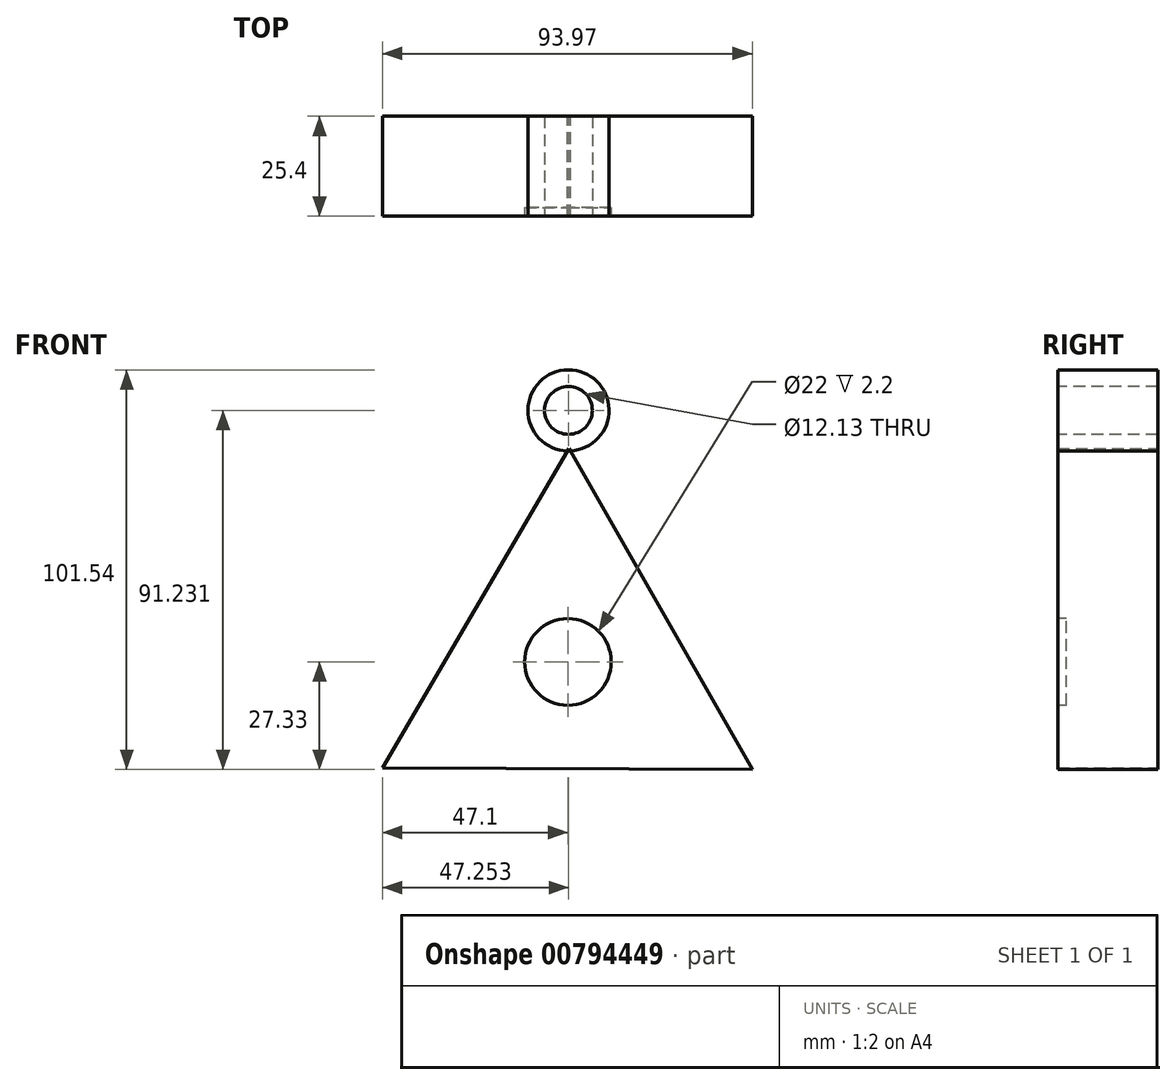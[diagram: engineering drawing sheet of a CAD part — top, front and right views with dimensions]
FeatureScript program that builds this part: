
annotation { "Feature Type Name" : "Feature", "Feature Type Description" : "" }
export const myFeature = defineFeature(function(context is Context, id is Id, definition is map)
    precondition{}
    {
        {
            var Q0;
            Q0=qCreatedBy(makeId("Front.planeOp"),FACE);
            var sketch = newSketch(context, id + "F0", { "sketchPlane" : qUnion([Q0])});
            skCircle(sketch, "E0.cCircle", {"center": v(0, 0) * mm, "radius": 27.13 * mm, "construction": true});
            skLineSegment(sketch, "E0.0", {"start": v(0.23, 54.25) * mm, "end": v(46.87, -27.33) * mm});
            skLineSegment(sketch, "E0.1", {"start": v(46.87, -27.33) * mm, "end": v(-47.1, -26.93) * mm});
            skLineSegment(sketch, "E0.2", {"start": v(-47.1, -26.93) * mm, "end": v(0.23, 54.25) * mm});
            skPoint(sketch, "E0.0.midPoint", {"position": v(23.55, 13.46) * mm});
            skCircle(sketch, "E1", {"center": v(0.15, 63.9) * mm, "radius": 10.3 * mm});
            skSolve(sketch);
        }
        {
            var Q0;
            Q0=makeQuery(id+"F0.imprint","IMPRINT",FACE,{"disambiguationData":[TD([[makeQuery(id+"F0.imprint","IMPRINT",EDGE,{"derivedFrom":sQuery(id+"F0.wireOp",EDGE,"E0.0")}),-1.0]])]});
            extrude(context, id + "F1", {"entities" : qUnion([Q0]), "depth" : 25.4 * mm, "offsetDistance" : 25.4 * mm});
        }
        {
            var Q0;
            Q0=makeQuery(id+"F1.opExtrude","CAP_FACE",FACE,{"disambiguationData":[OSD([sQuery(id+"F0.wireOp",EDGE,"E0.0"),sQuery(id+"F0.wireOp",EDGE,"E0.1"),sQuery(id+"F0.wireOp",EDGE,"E0.2")])],"isStart":false});
            var sketch = newSketch(context, id + "F2", { "sketchPlane" : qUnion([Q0])});
            skCircle(sketch, "E2", {"center": v(0, 0) * mm, "radius": 11 * mm});
            skSolve(sketch);
        }
        {
            var Q0;
            Q0=makeQuery(id+"F2.imprint","IMPRINT",FACE,{"disambiguationData":[TD([[makeQuery(id+"F2.imprint","IMPRINT",EDGE,{"derivedFrom":sQuery(id+"F2.wireOp",EDGE,"E2")}),1.0]])]});
            extrude(context, id + "F3", {"entities" : qUnion([Q0]), "operationType" : NewBodyOperationType.REMOVE, "oppositeDirection" : true, "depth" : 2.5 * mm, "offsetDistance" : 25.4 * mm});
        }
        {
            var Q0;
            Q0=makeQuery(id+"F1.opExtrude","CAP_FACE",FACE,{"disambiguationData":[OSD([sQuery(id+"F0.wireOp",EDGE,"E0.0"),sQuery(id+"F0.wireOp",EDGE,"E0.1"),sQuery(id+"F0.wireOp",EDGE,"E0.2")])],"isStart":false});
            var sketch = newSketch(context, id + "F4", { "sketchPlane" : qUnion([Q0])});
            skCircle(sketch, "E3", {"center": v(0, 0) * mm, "radius": 11 * mm});
            skSolve(sketch);
        }
        {
            var Q0;
            Q0=makeQuery(id+"F4.imprint","IMPRINT",FACE,{"disambiguationData":[TD([[makeQuery(id+"F4.imprint","IMPRINT",EDGE,{"derivedFrom":sQuery(id+"F4.wireOp",EDGE,"E3")}),1.0]])]});
            extrude(context, id + "F5", {"entities" : qUnion([Q0]), "operationType" : NewBodyOperationType.REMOVE, "oppositeDirection" : true, "depth" : 2.5 * mm, "offsetDistance" : 25.4 * mm});
        }
        {
            var Q0;
            Q0 = qSketchRegion(id + "F0", true);
            extrude(context, id + "F6", {"entities" : qUnion([Q0]), "depth" : 25.4 * mm, "offsetDistance" : 25.4 * mm});
        }
        {
            var Q0;
            Q0 = qSketchRegion(id + "F2", true);
            extrude(context, id + "F7", {"entities" : qUnion([Q0]), "operationType" : NewBodyOperationType.REMOVE, "oppositeDirection" : true, "depth" : 2.2 * mm, "offsetDistance" : 25.4 * mm});
        }
        {
            var Q0;
            Q0=makeQuery(id+"F6.opExtrude","CAP_FACE",FACE,{"disambiguationData":[OSD([sQuery(id+"F0.wireOp",EDGE,"E0.0"),sQuery(id+"F0.wireOp",EDGE,"E0.1"),sQuery(id+"F0.wireOp",EDGE,"E0.2"),sQuery(id+"F0.wireOp",EDGE,"E1")])],"isStart":false});
            var sketch = newSketch(context, id + "F8", { "sketchPlane" : qUnion([Q0])});
            skCircle(sketch, "E4", {"center": v(0.15, 63.9) * mm, "radius": 6.07 * mm});
            skSolve(sketch);
        }
        {
            var Q0;
            Q0=makeQuery(id+"F8.imprint","IMPRINT",FACE,{"disambiguationData":[TD([[makeQuery(id+"F8.imprint","IMPRINT",EDGE,{"derivedFrom":sQuery(id+"F8.wireOp",EDGE,"E4")}),1.0]])]});
            extrude(context, id + "F9", {"entities" : qUnion([Q0]), "operationType" : NewBodyOperationType.REMOVE, "oppositeDirection" : true, "depth" : 25.4 * mm, "offsetDistance" : 25.4 * mm});
        }
    });
